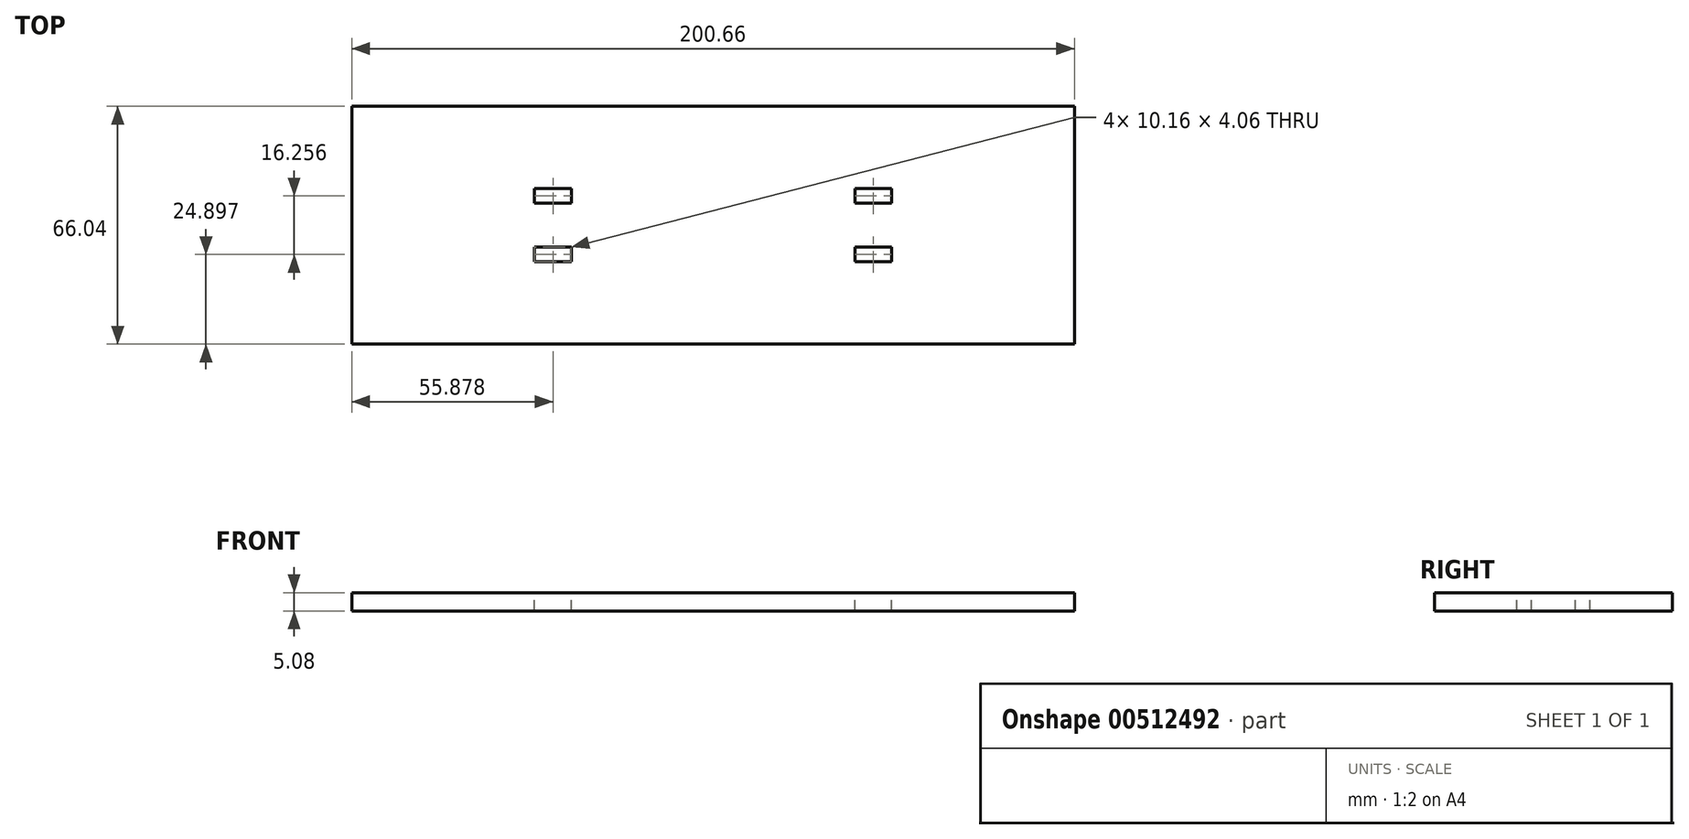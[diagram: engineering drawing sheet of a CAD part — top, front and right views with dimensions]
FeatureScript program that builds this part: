
annotation { "Feature Type Name" : "Feature", "Feature Type Description" : "" }
export const myFeature = defineFeature(function(context is Context, id is Id, definition is map)
    precondition{}
    {
        {
            var Q0;
            Q0=qCreatedBy(makeId("Top.planeOp"),FACE);
            var sketch = newSketch(context, id + "F0", { "sketchPlane" : qUnion([Q0])});
            skLineSegment(sketch, "E0.bottom", {"start": v(-56.92, 23.23) * mm, "end": v(143.74, 23.23) * mm});
            skLineSegment(sketch, "E0.top", {"start": v(-56.92, -42.8) * mm, "end": v(143.74, -42.8) * mm});
            skLineSegment(sketch, "E0.left", {"start": v(-56.92, 23.23) * mm, "end": v(-56.92, -42.8) * mm});
            skLineSegment(sketch, "E0.right", {"start": v(143.74, 23.23) * mm, "end": v(143.74, -42.8) * mm});
            skSolve(sketch);
        }
        {
            var Q0;
            Q0=makeQuery(id+"F0.imprint","IMPRINT",FACE,{"disambiguationData":[TD([[makeQuery(id+"F0.imprint","IMPRINT",EDGE,{"derivedFrom":sQuery(id+"F0.wireOp",EDGE,"E0.bottom")}),-1.0]])]});
            extrude(context, id + "F1", {"entities" : qUnion([Q0]), "depth" : 5.08 * mm});
        }
        {
            var Q0;
            Q0=makeQuery(id+"F1.opExtrude","CAP_FACE",FACE,{"disambiguationData":[OSD([sQuery(id+"F0.wireOp",EDGE,"E0.bottom"),sQuery(id+"F0.wireOp",EDGE,"E0.top"),sQuery(id+"F0.wireOp",EDGE,"E0.left"),sQuery(id+"F0.wireOp",EDGE,"E0.right")])],"isStart":false});
            var sketch = newSketch(context, id + "F2", { "sketchPlane" : qUnion([Q0])});
            skLineSegment(sketch, "E1.bottom", {"start": v(-6.12, 0.37) * mm, "end": v(4.04, 0.37) * mm});
            skLineSegment(sketch, "E1.top", {"start": v(-6.12, -3.69) * mm, "end": v(4.04, -3.69) * mm});
            skLineSegment(sketch, "E1.left", {"start": v(-6.12, 0.37) * mm, "end": v(-6.12, -3.69) * mm});
            skLineSegment(sketch, "E1.right", {"start": v(4.04, 0.37) * mm, "end": v(4.04, -3.69) * mm});
            skLineSegment(sketch, "E2.bottom", {"start": v(-6.12, -15.88) * mm, "end": v(4.04, -15.88) * mm});
            skLineSegment(sketch, "E2.top", {"start": v(-6.12, -19.95) * mm, "end": v(4.04, -19.95) * mm});
            skLineSegment(sketch, "E2.left", {"start": v(-6.12, -15.88) * mm, "end": v(-6.12, -19.95) * mm});
            skLineSegment(sketch, "E2.right", {"start": v(4.04, -15.88) * mm, "end": v(4.04, -19.95) * mm});
            skLineSegment(sketch, "E3.bottom", {"start": v(82.78, 0.37) * mm, "end": v(92.94, 0.37) * mm});
            skLineSegment(sketch, "E3.top", {"start": v(82.78, -3.69) * mm, "end": v(92.94, -3.69) * mm});
            skLineSegment(sketch, "E3.left", {"start": v(82.78, 0.37) * mm, "end": v(82.78, -3.69) * mm});
            skLineSegment(sketch, "E3.right", {"start": v(92.94, 0.37) * mm, "end": v(92.94, -3.69) * mm});
            skLineSegment(sketch, "E4.bottom", {"start": v(82.78, -15.88) * mm, "end": v(92.94, -15.88) * mm});
            skLineSegment(sketch, "E4.top", {"start": v(82.78, -19.95) * mm, "end": v(92.94, -19.95) * mm});
            skLineSegment(sketch, "E4.left", {"start": v(82.78, -15.88) * mm, "end": v(82.78, -19.95) * mm});
            skLineSegment(sketch, "E4.right", {"start": v(92.94, -15.88) * mm, "end": v(92.94, -19.95) * mm});
            skSolve(sketch);
        }
        {
            var Q0;
            Q0=makeQuery(id+"F2.imprint","IMPRINT",FACE,{"disambiguationData":[TD([[makeQuery(id+"F2.imprint","IMPRINT",EDGE,{"derivedFrom":sQuery(id+"F2.wireOp",EDGE,"E1.bottom")}),-1.0]])]});
            var Q1;
            Q1=makeQuery(id+"F2.imprint","IMPRINT",FACE,{"disambiguationData":[TD([[makeQuery(id+"F2.imprint","IMPRINT",EDGE,{"derivedFrom":sQuery(id+"F2.wireOp",EDGE,"E2.bottom")}),-1.0]])]});
            var Q2;
            Q2=makeQuery(id+"F2.imprint","IMPRINT",FACE,{"disambiguationData":[TD([[makeQuery(id+"F2.imprint","IMPRINT",EDGE,{"derivedFrom":sQuery(id+"F2.wireOp",EDGE,"E4.bottom")}),-1.0]])]});
            var Q3;
            Q3=makeQuery(id+"F2.imprint","IMPRINT",FACE,{"disambiguationData":[TD([[makeQuery(id+"F2.imprint","IMPRINT",EDGE,{"derivedFrom":sQuery(id+"F2.wireOp",EDGE,"E3.bottom")}),-1.0]])]});
            extrude(context, id + "F3", {"entities" : qUnion([Q0, Q1, Q2, Q3]), "operationType" : NewBodyOperationType.REMOVE, "oppositeDirection" : true, "depth" : 25.4 * mm});
        }
    });
